# Revit family: Комби-клапан – регулятор расхода F_4006
name_source: partatom
category: Rohrzubehör
revit_build: Autodesk Revit 2018 (Build: 20190510_1515(x64)
units: mm (PartAtom-declared; Revit-internal decimal feet)

## family parameters
Arbeitsebenenbasiert = Nein
Beim Laden mit Abzugskörper schneiden = Nein
Bemaßung runder Anschluss = Durchmesser verwenden
Gemeinsam genutzt = Nein
Immer vertikal = Ja
OmniClass-Nummer = 23.65.55.14
OmniClass-Titel = Valves for Liquid Services
Teiletyp = Unterbricht

## types (1)
- Комби-клапан – регулятор расхода F_4006
    D03 = 21 mm  [stored 0.0688976 ft]
    D07 = 30 mm  [stored 0.0984252 ft]
    D08 = 24 mm  [stored 0.0787402 ft]
    D13 = 16 mm  [stored 0.0524934 ft]
    D14 = 17 mm  [stored 0.0557743 ft]
    D15 = 5 mm  [stored 0.0164042 ft]
    D16 = 10 mm  [stored 0.0328084 ft]
    D17 = 3 mm  [stored 0.00984252 ft]
    D18 = 4 mm  [stored 0.0131234 ft]
    H04 = 5 mm  [stored 0.0164042 ft]
    H05 = 3 mm  [stored 0.00984252 ft]
    H08 = 21 mm  [stored 0.0688976 ft]
    H16 = 3 mm  [stored 0.00984252 ft]
    H17 = 5 mm  [stored 0.0164042 ft]
    H18 = 4 mm  [stored 0.0131234 ft]
    Hersteller = Herz-Armaturen GmbH
    K00 = 24 mm  [stored 0.0787402 ft]
    K01 = 4 mm  [stored 0.0131234 ft]
    K02 = 5 mm  [stored 0.0164042 ft]
    K03 = 14 mm  [stored 0.0459318 ft]
    L01 = 3 mm  [stored 0.00984252 ft]
    L03 = 10 mm  [stored 0.0328084 ft]
    M00 = 27 mm  [stored 0.0885827 ft]
    M01 = 9 mm  [stored 0.0295276 ft]
    M02 = 6 mm  [stored 0.019685 ft]
    M03 = 3 mm  [stored 0.00984252 ft]
    M04 = 2 mm  [stored 0.00656168 ft]
    M05 = 4 mm  [stored 0.0131234 ft]
    R02 = 13 mm
    R03 = 7 mm  [stored 0.0229659 ft]
    R04 = 8 mm  [stored 0.0262467 ft]
    R05 = 5 mm  [stored 0.0164042 ft]
    R97 = 2 mm  [stored 0.00656168 ft]
    R98 = 6 mm  [stored 0.019685 ft]
    R99 = 14 mm  [stored 0.0459318 ft]
    SCRNCODE = 05;04;02
    SCRNSEQ = ARM;ARM_TYP="DURR";2
    URL = www.herz-armaturen.ru
    Импульсная трубка = WN1.4301
    Конус = CW617N-R320-S
    Корпус = EN-GJL-250
    Макс. перепад давления = 400000.0 Pa
    Макс. рабочая температура = 110 °C
    Максимальное рабочее давление = 1600000.0 Pa
    Мембрана = EPDM
    Мин. рабочая температура (с антифризом) = -20 °C
    Мин. рабочая температура (чистая вода) = 2 °C
    Область применения = Комби-клапан применяется в системах отопления и охлаждения с насосами. Комби-клапан автоматически ограничивает расход на выбранном участке системы до заданного значения, компенсируя все колебания давления. При этом нет необходимости в измерениях, а регулирование эффективно при любых условиях эксплуатации. Комби-клапан регулирует расход в соответствии с настройкой до заданного значения; на мембрану воздействует давление непосредственно до и после регулирующей части.
    Перепад давления на oграничителе расхода = 20000.0 Pa
    Седло = WN1.4305
    Среда = Качество теплоносителя в соответствии с ÖNORM H5195 и/или предписаниями VDI-Standard 2035.
Разрешается использование смеси этилен- или пропиленгликоля в соотношении 25-50% с водой.
    Уплотнения = EPDM
    Фланцевое соединение = EN 1092-2
    Шпиндель = WN1.4305

note: [stored X ft] marks values corroborated as IEEE doubles in the binary element streams (Revit-internal decimal feet)
